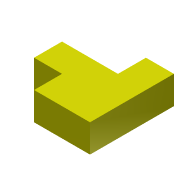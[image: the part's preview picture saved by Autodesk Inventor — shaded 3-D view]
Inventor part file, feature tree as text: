
AUTODESK INVENTOR PART (.ipt)
format: ipt  version: 2015 (Build 190159000, 159)  size: 80,384 bytes
history: native  units: in
note: dims shown in document units (in); Inventor stores cm internally (conversion verified against a paired STEP export)
features: extrude x1, sketch x1
ambient origin geometry x8: Origin, YZ Plane, XZ Plane, XY Plane, X Axis, Y Axis, Z Axis, Center Point
bodies: Solid1 (feature_tree)
feature tree (2):
  extrude  "Extrusion1"  Depth=1.0in
  sketch  "Sketch1"  dims[d0=2.0in d1=1.0in d2=1.0in d3=1.0in d4=1.0in d5=2.0in d6=1.0in d7=0.0in]
